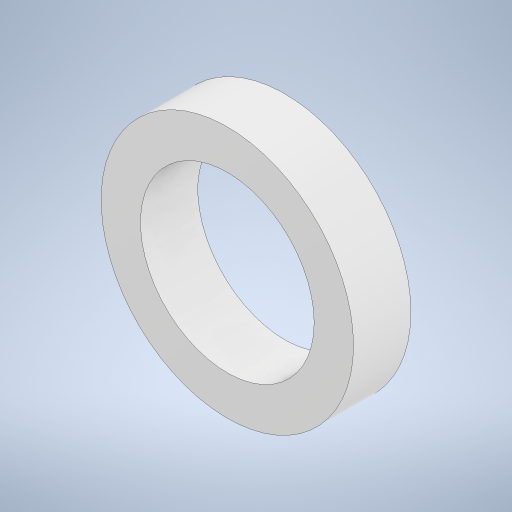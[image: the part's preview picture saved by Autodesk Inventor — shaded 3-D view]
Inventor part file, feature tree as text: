
AUTODESK INVENTOR PART (.ipt)
format: ipt  version: 2024 (Build 280153000, 153)  size: 225,280 bytes
history: native  units: mm
features: extrude x1, sketch x1
ambient origin geometry x8: Origin, YZ Plane, XZ Plane, XY Plane, X Axis, Y Axis, Z Axis, Center Point
bodies: Solid1 (feature_tree)
feature tree (2):
  extrude  "Extrusion1"  Depth=1.75mm
  sketch  "Sketch1"  dims[d0=5.3mm d1=1.2mm d2=1.75mm d3=0.0mm]
